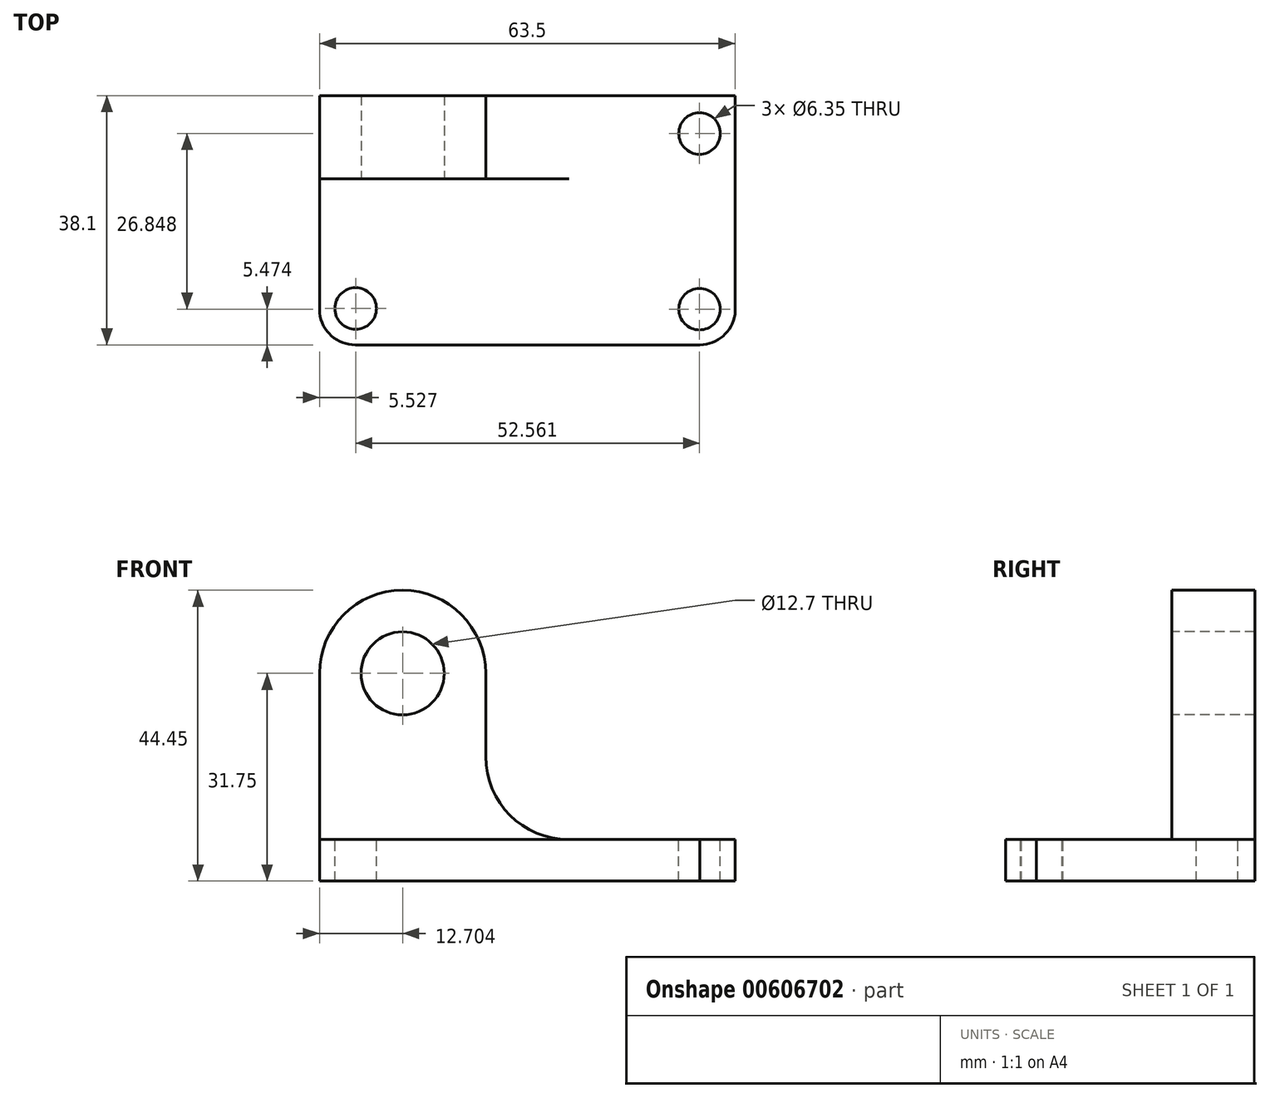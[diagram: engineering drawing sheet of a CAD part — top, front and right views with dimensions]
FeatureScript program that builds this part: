
annotation { "Feature Type Name" : "Feature", "Feature Type Description" : "" }
export const myFeature = defineFeature(function(context is Context, id is Id, definition is map)
    precondition{}
    {
        {
            var Q0;
            Q0=qCreatedBy(makeId("Front.planeOp"),FACE);
            var sketch = newSketch(context, id + "F0", { "sketchPlane" : qUnion([Q0])});
            skLineSegment(sketch, "E0", {"start": v(-66.19, 0) * mm, "end": v(-66.19, 44.45) * mm});
            skLineSegment(sketch, "E1", {"start": v(-66.19, 44.45) * mm, "end": v(-2.69, 44.45) * mm});
            skLineSegment(sketch, "E2", {"start": v(-2.69, 44.45) * mm, "end": v(-2.69, 0) * mm});
            skLineSegment(sketch, "E3", {"start": v(-2.69, 0) * mm, "end": v(-66.19, 0) * mm});
            skSolve(sketch);
        }
        {
            var Q0;
            Q0=makeQuery(id+"F0.imprint","IMPRINT",FACE,{"disambiguationData":[TD([[makeQuery(id+"F0.imprint","IMPRINT",EDGE,{"derivedFrom":sQuery(id+"F0.wireOp",EDGE,"E0")}),-1.0]])]});
            extrude(context, id + "F1", {"entities" : qUnion([Q0]), "depth" : 38.1 * mm, "offsetDistance" : 25.4 * mm});
        }
        {
            var Q0;
            Q0=makeQuery(id+"F1.opExtrude","SWEPT_FACE",FACE,{"disambiguationData":[OSD([sQuery(id+"F0.wireOp",EDGE,"E0")])]});
            var sketch = newSketch(context, id + "F2", { "sketchPlane" : qUnion([Q0])});
            skLineSegment(sketch, "E4", {"start": v(38.1, 0) * mm, "end": v(38.1, 6.35) * mm});
            skLineSegment(sketch, "E5", {"start": v(38.1, 6.35) * mm, "end": v(12.7, 6.35) * mm});
            skLineSegment(sketch, "E6", {"start": v(12.7, 6.35) * mm, "end": v(12.7, 44.45) * mm});
            skLineSegment(sketch, "E7", {"start": v(12.7, 44.45) * mm, "end": v(0, 44.45) * mm});
            skSolve(sketch);
        }
        {
            var Q0;
            {var subQ0=sQuery(id+"F2.wireOp",EDGE,"E5");Q0=makeQuery(id+"F2.imprint","IMPRINT",FACE,{"disambiguationData":[TD([[makeQuery(id+"F2.imprint","IMPRINT",EDGE,{"derivedFrom":subQ0}),-1.0]])]});}
            extrude(context, id + "F3", {"entities" : qUnion([Q0]), "operationType" : NewBodyOperationType.REMOVE, "oppositeDirection" : true, "depth" : 63.5 * mm, "offsetDistance" : 25.4 * mm});
        }
        {
            var Q0;
            Q0=makeQuery(id+"F3.boolean.opBoolean","COPY",FACE,{"derivedFrom":makeQuery(id+"F3.opExtrude","SWEPT_FACE",FACE,{"disambiguationData":[OSD([sQuery(id+"F2.wireOp",EDGE,"E6")])]})});
            var sketch = newSketch(context, id + "F4", { "sketchPlane" : qUnion([Q0])});
            skLineSegment(sketch, "E8", {"start": v(-2.69, 44.45) * mm, "end": v(-28.09, 44.45) * mm});
            skLineSegment(sketch, "E9", {"start": v(-28.09, 44.45) * mm, "end": v(-28.09, 6.35) * mm});
            skLineSegment(sketch, "E10", {"start": v(-28.09, 6.35) * mm, "end": v(-2.69, 6.35) * mm});
            skLineSegment(sketch, "E11", {"start": v(-2.69, 6.35) * mm, "end": v(-2.69, 44.45) * mm});
            skSolve(sketch);
        }
        {
            var Q0;
            Q0=makeQuery(id+"F4.imprint","IMPRINT",FACE,{"disambiguationData":[TD([[makeQuery(id+"F4.imprint","IMPRINT",EDGE,{"derivedFrom":sQuery(id+"F4.wireOp",EDGE,"E8")}),1.0]])]});
            extrude(context, id + "F5", {"entities" : qUnion([Q0]), "operationType" : NewBodyOperationType.REMOVE, "oppositeDirection" : true, "depth" : 12.7 * mm, "offsetDistance" : 25.4 * mm});
        }
        {
            var Q0;
            Q0=makeQuery(id+"F3.boolean.opBoolean","COPY",FACE,{"derivedFrom":makeQuery(id+"F3.opExtrude","SWEPT_FACE",FACE,{"disambiguationData":[OSD([sQuery(id+"F2.wireOp",EDGE,"E6")])]})});
            var sketch = newSketch(context, id + "F6", { "sketchPlane" : qUnion([Q0])});
            skArc(sketch, "E12", {"start": v(-40.79, 19.05) * mm, "mid": v(-37.07, 10.07) * mm, "end": v(-28.09, 6.35) * mm});
            skLineSegment(sketch, "E13", {"start": v(-40.79, 19.05) * mm, "end": v(-40.79, 44.45) * mm});
            skSolve(sketch);
        }
        {
            var Q0;
            Q0=makeQuery(id+"F6.imprint","IMPRINT",FACE,{"disambiguationData":[TD([[makeQuery(id+"F6.imprint","IMPRINT",EDGE,{"derivedFrom":sQuery(id+"F6.wireOp",EDGE,"E12")}),1.0]])]});
            extrude(context, id + "F7", {"entities" : qUnion([Q0]), "operationType" : NewBodyOperationType.REMOVE, "oppositeDirection" : true, "depth" : 12.7 * mm, "offsetDistance" : 25.4 * mm});
        }
        {
            var Q0;
            Q0=makeQuery(id+"F3.boolean.opBoolean","COPY",FACE,{"derivedFrom":makeQuery(id+"F3.opExtrude","SWEPT_FACE",FACE,{"disambiguationData":[OSD([sQuery(id+"F2.wireOp",EDGE,"E6")])]})});
            var sketch = newSketch(context, id + "F8", { "sketchPlane" : qUnion([Q0])});
            skLineSegment(sketch, "E14", {"start": v(-40.79, 31.75) * mm, "end": v(-40.79, 19.05) * mm});
            skArc(sketch, "E15", {"start": v(-40.79, 31.75) * mm, "mid": v(-53.49, 44.45) * mm, "end": v(-66.19, 31.75) * mm});
            skSolve(sketch);
        }
        {
            var Q0;
            {var subQ0=sQuery(id+"F8.wireOp",EDGE,"E15");var subQ1=sQuery(id+"F2.wireOp",EDGE,"E6");var subQ2=makeQuery(id+"F3.boolean.opBoolean","COPY",EDGE,{"derivedFrom":makeQuery(id+"F3.opExtrude","CAP_EDGE",EDGE,{"disambiguationData":[OSD([subQ1])],"isStart":true})});var subQ3=makeQuery(id+"F8.imprint","INTERSECT",VERTEX,{"derivedFrom":[subQ2,subQ0]});Q0=makeQuery(id+"F8.imprint","IMPRINT",FACE,{"disambiguationData":[TD([[makeQuery(id+"F8.imprint","IMPRINT",EDGE,{"disambiguationData":[TD([[subQ3,1.0]])],"derivedFrom":subQ0}),-1.0]])]});}
            var Q1;
            {var subQ0=sQuery(id+"F8.wireOp",EDGE,"E15");var subQ1=makeQuery(id+"F7.boolean.opBoolean","COPY",EDGE,{"derivedFrom":makeQuery(id+"F7.opExtrude","CAP_EDGE",EDGE,{"disambiguationData":[OSD([sQuery(id+"F6.wireOp",EDGE,"E13")])],"isStart":true})});var subQ2=makeQuery(id+"F8.imprint","INTERSECT",VERTEX,{"derivedFrom":[subQ1,sQuery(id+"F8.wireOp",EDGE,"E14"),subQ0]});Q1=makeQuery(id+"F8.imprint","IMPRINT",FACE,{"disambiguationData":[TD([[makeQuery(id+"F8.imprint","IMPRINT",EDGE,{"disambiguationData":[TD([[subQ2,-1.0]])],"derivedFrom":subQ0}),-1.0]])]});}
            extrude(context, id + "F9", {"entities" : qUnion([Q0, Q1]), "operationType" : NewBodyOperationType.REMOVE, "oppositeDirection" : true, "depth" : 12.7 * mm, "offsetDistance" : 25.4 * mm});
        }
        {
            var Q0;
            Q0=makeQuery(id+"F3.boolean.opBoolean","COPY",FACE,{"derivedFrom":makeQuery(id+"F3.opExtrude","SWEPT_FACE",FACE,{"disambiguationData":[OSD([sQuery(id+"F2.wireOp",EDGE,"E6")])]})});
            var sketch = newSketch(context, id + "F10", { "sketchPlane" : qUnion([Q0])});
            skCircle(sketch, "E16", {"center": v(-53.49, 31.75) * mm, "radius": 6.35 * mm});
            skSolve(sketch);
        }
        {
            var Q0;
            Q0=makeQuery(id+"F10.imprint","IMPRINT",FACE,{"disambiguationData":[TD([[makeQuery(id+"F10.imprint","IMPRINT",EDGE,{"derivedFrom":sQuery(id+"F10.wireOp",EDGE,"E16")}),1.0]])]});
            extrude(context, id + "F11", {"entities" : qUnion([Q0]), "operationType" : NewBodyOperationType.REMOVE, "oppositeDirection" : true, "depth" : 12.7 * mm, "offsetDistance" : 25.4 * mm});
        }
        {
            var Q0;
            Q0=makeQuery(id+"F5.boolean.opBoolean","MERGE",FACE,{"derivedFrom":[makeQuery(id+"F3.boolean.opBoolean","COPY",FACE,{"derivedFrom":makeQuery(id+"F3.opExtrude","SWEPT_FACE",FACE,{"disambiguationData":[OSD([sQuery(id+"F2.wireOp",EDGE,"E5")])]})}),makeQuery(id+"F5.opExtrude","SWEPT_FACE",FACE,{"disambiguationData":[OSD([sQuery(id+"F4.wireOp",EDGE,"E10")])]})]});
            var sketch = newSketch(context, id + "F12", { "sketchPlane" : qUnion([Q0])});
            skArc(sketch, "E17", {"start": v(-66.19, -31.82) * mm, "mid": v(-64.85, -36.2) * mm, "end": v(-60.7, -38.1) * mm});
            skArc(sketch, "E18", {"start": v(-8.04, -38.1) * mm, "mid": v(-3.94, -36.18) * mm, "end": v(-2.69, -31.82) * mm});
            skSolve(sketch);
        }
        {
            var Q0;
            {var subQ0=sQuery(id+"F12.wireOp",EDGE,"E17");var subQ1=sQuery(id+"F2.wireOp",EDGE,"E5");var subQ4=makeQuery(id+"F3.boolean.opBoolean","COPY",EDGE,{"derivedFrom":makeQuery(id+"F3.opExtrude","CAP_EDGE",EDGE,{"disambiguationData":[OSD([subQ1])],"isStart":true})});var subQ5=makeQuery(id+"F12.imprint","INTERSECT",VERTEX,{"disambiguationData":[OD(1.0)],"derivedFrom":[subQ4,subQ0]});Q0=makeQuery(id+"F12.imprint","IMPRINT",FACE,{"disambiguationData":[TD([[makeQuery(id+"F12.imprint","IMPRINT",EDGE,{"disambiguationData":[TD([[subQ5,-1.0]])],"derivedFrom":subQ0}),-1.0]])]});}
            var Q1;
            {var subQ0=sQuery(id+"F12.wireOp",EDGE,"E18");var subQ1=sQuery(id+"F2.wireOp",EDGE,"E5");var subQ2=makeQuery(id+"F3.boolean.opBoolean","COPY",EDGE,{"derivedFrom":makeQuery(id+"F3.opExtrude","SWEPT_EDGE",EDGE,{"disambiguationData":[OSD([sQuery(id+"F0.wireOp",EDGE,"E0"),sQuery(id+"F2.wireOp",EDGE,"E4"),subQ1])]})});var subQ3=makeQuery(id+"F12.imprint","INTERSECT",VERTEX,{"derivedFrom":[subQ2,subQ0]});Q1=makeQuery(id+"F12.imprint","IMPRINT",FACE,{"disambiguationData":[TD([[makeQuery(id+"F12.imprint","IMPRINT",EDGE,{"disambiguationData":[TD([[subQ3,-1.0]])],"derivedFrom":subQ0}),-1.0]])]});}
            extrude(context, id + "F13", {"entities" : qUnion([Q0, Q1]), "operationType" : NewBodyOperationType.REMOVE, "oppositeDirection" : true, "depth" : 6.35 * mm, "offsetDistance" : 25.4 * mm});
        }
        {
            var Q0;
            Q0=makeQuery(id+"F5.boolean.opBoolean","MERGE",FACE,{"derivedFrom":[makeQuery(id+"F3.boolean.opBoolean","COPY",FACE,{"derivedFrom":makeQuery(id+"F3.opExtrude","SWEPT_FACE",FACE,{"disambiguationData":[OSD([sQuery(id+"F2.wireOp",EDGE,"E5")])]})}),makeQuery(id+"F5.opExtrude","SWEPT_FACE",FACE,{"disambiguationData":[OSD([sQuery(id+"F4.wireOp",EDGE,"E10")])]})]});
            var sketch = newSketch(context, id + "F14", { "sketchPlane" : qUnion([Q0])});
            skCircle(sketch, "E19", {"center": v(-60.66, -32.53) * mm, "radius": 3.17 * mm});
            skCircle(sketch, "E20", {"center": v(-8.1, -32.63) * mm, "radius": 3.18 * mm});
            skCircle(sketch, "E21", {"center": v(-8.1, -5.78) * mm, "radius": 3.18 * mm});
            skSolve(sketch);
        }
        {
            var Q0;
            Q0=makeQuery(id+"F14.imprint","IMPRINT",FACE,{"disambiguationData":[TD([[makeQuery(id+"F14.imprint","IMPRINT",EDGE,{"derivedFrom":sQuery(id+"F14.wireOp",EDGE,"E19")}),1.0]])]});
            var Q1;
            Q1=makeQuery(id+"F14.imprint","IMPRINT",FACE,{"disambiguationData":[TD([[makeQuery(id+"F14.imprint","IMPRINT",EDGE,{"derivedFrom":sQuery(id+"F14.wireOp",EDGE,"E20")}),1.0]])]});
            var Q2;
            Q2=makeQuery(id+"F14.imprint","IMPRINT",FACE,{"disambiguationData":[TD([[makeQuery(id+"F14.imprint","IMPRINT",EDGE,{"derivedFrom":sQuery(id+"F14.wireOp",EDGE,"E21")}),1.0]])]});
            extrude(context, id + "F15", {"entities" : qUnion([Q0, Q1, Q2]), "operationType" : NewBodyOperationType.REMOVE, "oppositeDirection" : true, "depth" : 6.35 * mm, "offsetDistance" : 25.4 * mm});
        }
    });
